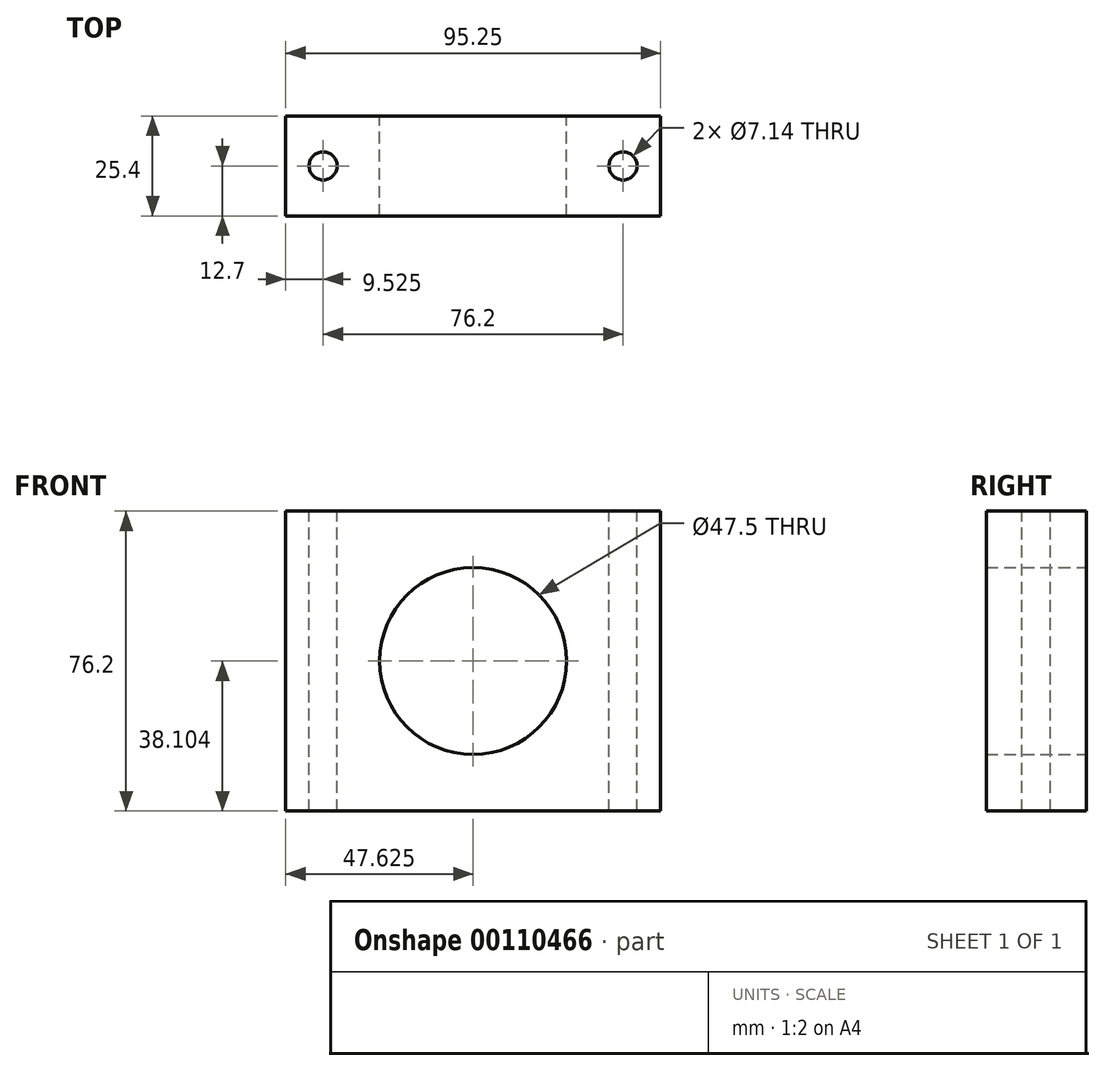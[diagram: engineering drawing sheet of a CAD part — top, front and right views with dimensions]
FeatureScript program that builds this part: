
annotation { "Feature Type Name" : "Feature", "Feature Type Description" : "" }
export const myFeature = defineFeature(function(context is Context, id is Id, definition is map)
    precondition{}
    {
        {
            var Q0;
            Q0=qCreatedBy(makeId("Front.planeOp"),FACE);
            var sketch = newSketch(context, id + "F0", { "sketchPlane" : qUnion([Q0])});
            skLineSegment(sketch, "E0.bottom", {"start": v(-56.2, 45.37) * mm, "end": v(39.06, 45.37) * mm});
            skLineSegment(sketch, "E0.top", {"start": v(-56.2, -30.83) * mm, "end": v(39.06, -30.83) * mm});
            skLineSegment(sketch, "E0.left", {"start": v(-56.2, 45.37) * mm, "end": v(-56.2, -30.83) * mm});
            skLineSegment(sketch, "E0.right", {"start": v(39.06, 45.37) * mm, "end": v(39.06, -30.83) * mm});
            skCircle(sketch, "E1", {"center": v(-8.57, 7.27) * mm, "radius": 23.75 * mm});
            skPoint(sketch, "E1.centerSnap0", {"position": v(-56.2, 7.27) * mm});
            skPoint(sketch, "E1.centerSnap1", {"position": v(-8.57, 45.37) * mm});
            skSolve(sketch);
        }
        {
            var Q0;
            Q0 = qSketchRegion(id + "F0", true);
            extrude(context, id + "F1", {"entities" : qUnion([Q0]), "depth" : 25.4 * mm});
        }
        {
            var Q0;
            Q0=makeQuery(id+"F1.opExtrude","SWEPT_FACE",FACE,{"disambiguationData":[OSD([sQuery(id+"F0.wireOp",EDGE,"E0.bottom")])]});
            var sketch = newSketch(context, id + "F2", { "sketchPlane" : qUnion([Q0])});
            skCircle(sketch, "E2", {"center": v(-46.67, -12.7) * mm, "radius": 3.57 * mm});
            skPoint(sketch, "E2.centerSnap0", {"position": v(-56.2, -12.7) * mm});
            skPoint(sketch, "E3.centerSnap0", {"position": v(39.06, -12.7) * mm});
            skLineSegment(sketch, "E4", {"start": v(39.06, 0) * mm, "end": v(39.06, -12.7) * mm, "construction": true});
            skLineSegment(sketch, "E5", {"start": v(39.06, -12.7) * mm, "end": v(29.53, -12.7) * mm});
            skCircle(sketch, "E6", {"center": v(29.53, -12.7) * mm, "radius": 3.57 * mm});
            skSolve(sketch);
        }
        {
            var Q0;
            Q0=makeQuery(id+"F2.imprint","IMPRINT",FACE,{"disambiguationData":[TD([[makeQuery(id+"F2.imprint","IMPRINT",EDGE,{"derivedFrom":sQuery(id+"F2.wireOp",EDGE,"E2")}),1.0]])]});
            var Q1;
            Q1=makeQuery(id+"F2.imprint","IMPRINT",FACE,{"disambiguationData":[TD([[makeQuery(id+"F2.imprint","IMPRINT",EDGE,{"derivedFrom":sQuery(id+"F2.wireOp",EDGE,"E3")}),1.0]])]});
            extrude(context, id + "F3", {"entities" : qUnion([Q0, Q1]), "operationType" : NewBodyOperationType.REMOVE, "endBound" : BoundingType.THROUGH_ALL, "oppositeDirection" : true, "depth" : 25.4 * mm});
        }
        {
            var Q0;
            Q0 = qSketchRegion(id + "F2", true);
            var Q1;
            Q1=sQuery(id+"F2.wireOp",EDGE,"E6");
            var Q2;
            Q2=sQuery(id+"F2.wireOp",EDGE,"E2");
            extrude(context, id + "F4", {"entities" : qUnion([Q0]), "operationType" : NewBodyOperationType.REMOVE, "surfaceEntities" : qUnion([Q1, Q2]), "endBound" : BoundingType.THROUGH_ALL, "oppositeDirection" : true, "depth" : 25.4 * mm});
        }
    });
